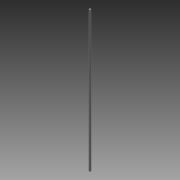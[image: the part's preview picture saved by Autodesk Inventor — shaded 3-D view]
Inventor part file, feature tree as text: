
AUTODESK INVENTOR PART (.ipt)
format: ipt  version: 2015 (Build 190159000, 159)  size: 62,976 bytes
history: native  units: in
note: dims shown in document units (in); Inventor stores cm internally (conversion verified against a paired STEP export)
features: extrude x1, sketch x1
ambient origin geometry x8: Origin, YZ Plane, XZ Plane, XY Plane, X Axis, Y Axis, Z Axis, Center Point
bodies: Solid1 (feature_tree)
feature tree (2):
  extrude  "Extrusion1"  Depth=10.0in TaperAngle=0.0deg
  sketch  "Sketch1"  dims[d0=0.125in d1=10.0in d2=0.0in]
